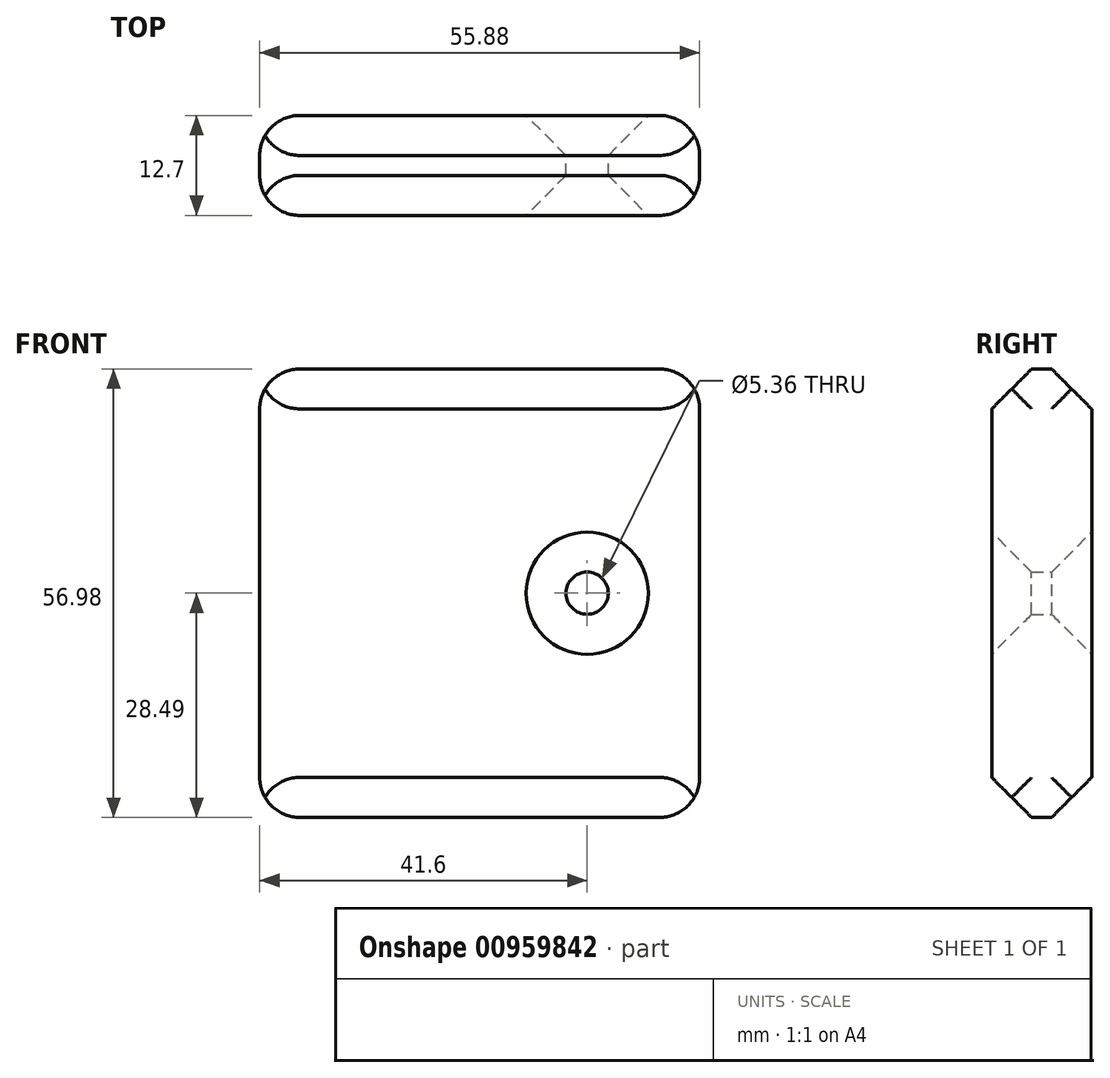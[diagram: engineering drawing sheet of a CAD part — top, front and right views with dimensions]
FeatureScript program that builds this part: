
annotation { "Feature Type Name" : "Feature", "Feature Type Description" : "" }
export const myFeature = defineFeature(function(context is Context, id is Id, definition is map)
    precondition{}
    {
        {
            var Q0;
            Q0=qCreatedBy(makeId("Front.planeOp"),FACE);
            var sketch = newSketch(context, id + "F0", { "sketchPlane" : qUnion([Q0])});
            skLineSegment(sketch, "E0.bottom", {"start": v(27.94, -28.49) * mm, "end": v(-27.94, -28.49) * mm});
            skLineSegment(sketch, "E0.top", {"start": v(27.94, 28.49) * mm, "end": v(-27.94, 28.49) * mm});
            skLineSegment(sketch, "E0.left", {"start": v(27.94, -28.49) * mm, "end": v(27.94, 28.49) * mm});
            skLineSegment(sketch, "E0.right", {"start": v(-27.94, -28.49) * mm, "end": v(-27.94, 28.49) * mm});
            skPoint(sketch, "E0.middle", {"position": v(0, 0) * mm});
            skCircle(sketch, "E1", {"center": v(13.66, 0) * mm, "radius": 2.68 * mm});
            skSolve(sketch);
        }
        {
            var Q0;
            Q0=makeQuery(id+"F0.imprint","IMPRINT",FACE,{"disambiguationData":[TD([[makeQuery(id+"F0.imprint","IMPRINT",EDGE,{"derivedFrom":sQuery(id+"F0.wireOp",EDGE,"E0.bottom")}),-1.0]])]});
            extrude(context, id + "F1", {"entities" : qUnion([Q0]), "endBound" : BoundingType.SYMMETRIC, "depth" : 12.7 * mm, "offsetDistance" : 25.4 * mm});
        }
        {
            var Q0;
            Q0=makeQuery(id+"F1.opExtrude","SWEPT_FACE",FACE,{"disambiguationData":[OSD([sQuery(id+"F0.wireOp",EDGE,"E0.right")])]});
            fillet(context, id + "F2", {"entities" : qUnion([Q0]), "radius" : 5.08 * mm, "tangentPropagation" : true, "allowEdgeOverflow" : false});
        }
        {
            var Q0;
            Q0=makeQuery(id+"F1.opExtrude","SWEPT_FACE",FACE,{"disambiguationData":[OSD([sQuery(id+"F0.wireOp",EDGE,"E0.left")])]});
            fillet(context, id + "F3", {"entities" : qUnion([Q0]), "radius" : 5.08 * mm, "tangentPropagation" : true, "allowEdgeOverflow" : false});
        }
        {
            var Q0;
            Q0=makeQuery(id+"F1.opExtrude","CAP_FACE",FACE,{"disambiguationData":[OSD([sQuery(id+"F0.wireOp",EDGE,"E0.bottom"),sQuery(id+"F0.wireOp",EDGE,"E0.top"),sQuery(id+"F0.wireOp",EDGE,"E0.left"),sQuery(id+"F0.wireOp",EDGE,"E0.right")])],"isStart":false});
            chamfer(context, id + "F4", {"entities" : qUnion([Q0]), "width" : 5.08 * mm, "tangentPropagation" : true});
        }
        {
            var Q0;
            Q0=makeQuery(id+"F1.opExtrude","CAP_FACE",FACE,{"disambiguationData":[OSD([sQuery(id+"F0.wireOp",EDGE,"E0.bottom"),sQuery(id+"F0.wireOp",EDGE,"E0.top"),sQuery(id+"F0.wireOp",EDGE,"E0.left"),sQuery(id+"F0.wireOp",EDGE,"E0.right")])],"isStart":true});
            chamfer(context, id + "F5", {"entities" : qUnion([Q0]), "width" : 5.08 * mm, "tangentPropagation" : true});
        }
    });
